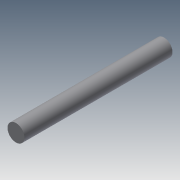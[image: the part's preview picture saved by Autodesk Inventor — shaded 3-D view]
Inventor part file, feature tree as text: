
AUTODESK INVENTOR PART (.ipt)
format: ipt  version: 2015 (Build 190159000, 159)  size: 73,728 bytes
history: native  units: mm
features: extrude x2, sketch x2
ambient origin geometry x8: Origin, YZ Plane, XZ Plane, XY Plane, X Axis, Y Axis, Z Axis, Center Point
bodies: Solid1 (feature_tree)
feature tree (4):
  extrude  "Extrusion1"  Depth=28.0mm TaperAngle=0.0deg
  extrude  "Extrusion2"  [1 undecoded]
  sketch  "Sketch1"  dims[d0=4.0mm d1=28.0mm d2=0.0mm]
  sketch  "Sketch2"  dims[d3=7.0mm d4=0.0mm]
note: 1 required parameter value undecoded (feature->parameter linkage not recoverable at this tier; creation-order binding heuristic only, values carry confidence <= 0.55)
